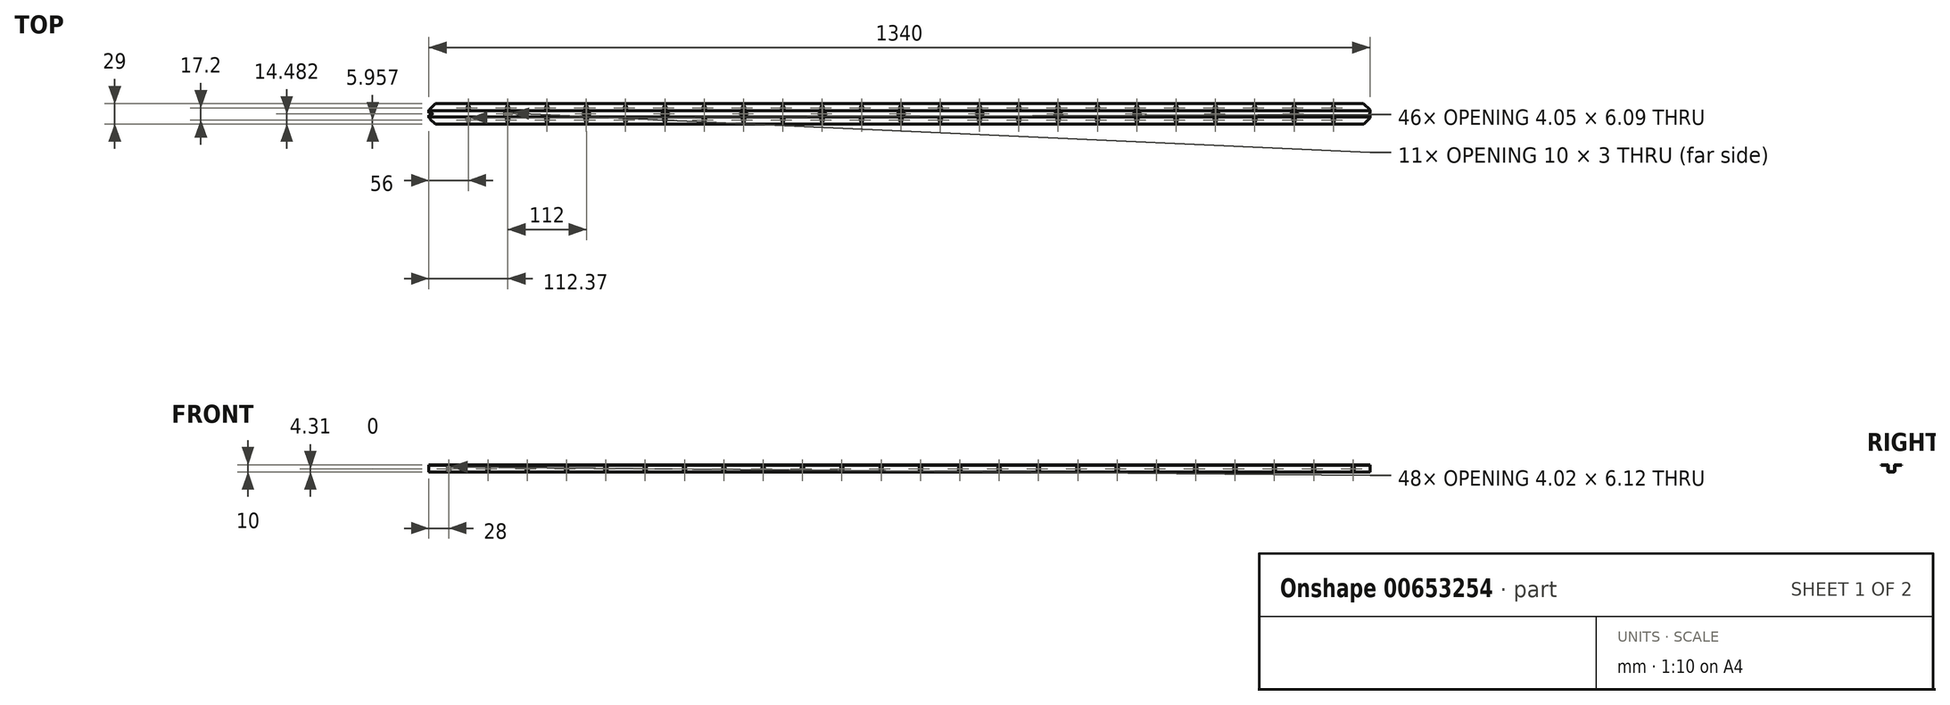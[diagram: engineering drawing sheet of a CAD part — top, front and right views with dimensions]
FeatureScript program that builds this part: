
annotation { "Feature Type Name" : "Feature", "Feature Type Description" : "" }
export const myFeature = defineFeature(function(context is Context, id is Id, definition is map)
    precondition{}
    {
        {
            var Q0;
            Q0=qCreatedBy(makeId("Right.planeOp"),FACE);
            var sketch = newSketch(context, id + "F0", { "sketchPlane" : qUnion([Q0])});
            skLineSegment(sketch, "E0", {"start": v(14.5, 5) * mm, "end": v(5.5, 5) * mm});
            skArc(sketch, "E1", {"start": v(5.5, 5) * mm, "mid": v(4.8, 4.7) * mm, "end": v(4.5, 4) * mm});
            skLineSegment(sketch, "E2", {"start": v(4.5, 4) * mm, "end": v(4.5, -4) * mm});
            skArc(sketch, "E3", {"start": v(4.5, -4) * mm, "mid": v(4.35, -4.35) * mm, "end": v(4, -4.5) * mm});
            skLineSegment(sketch, "E4", {"start": v(4, -4.5) * mm, "end": v(-4, -4.5) * mm});
            skArc(sketch, "E5", {"start": v(-4, -4.5) * mm, "mid": v(-4.35, -4.35) * mm, "end": v(-4.5, -4) * mm});
            skLineSegment(sketch, "E6", {"start": v(-4.5, -4) * mm, "end": v(-4.5, 4) * mm});
            skArc(sketch, "E7", {"start": v(-4.5, 4) * mm, "mid": v(-4.8, 4.7) * mm, "end": v(-5.5, 5) * mm});
            skLineSegment(sketch, "E8", {"start": v(-5.5, 5) * mm, "end": v(-14.5, 5) * mm});
            skLineSegment(sketch, "E9", {"start": v(-14.5, 5) * mm, "end": v(-14.5, 4.5) * mm});
            skLineSegment(sketch, "E10", {"start": v(-14.5, 4.5) * mm, "end": v(-5.5, 4.5) * mm});
            skArc(sketch, "E11", {"start": v(-5.5, 4.5) * mm, "mid": v(-5.15, 4.35) * mm, "end": v(-5, 4) * mm});
            skLineSegment(sketch, "E12", {"start": v(-5, 4) * mm, "end": v(-5, -4) * mm});
            skArc(sketch, "E13", {"start": v(-5, -4) * mm, "mid": v(-4.7, -4.7) * mm, "end": v(-4, -5) * mm});
            skLineSegment(sketch, "E14", {"start": v(-4, -5) * mm, "end": v(4, -5) * mm});
            skArc(sketch, "E15", {"start": v(4, -5) * mm, "mid": v(4.7, -4.7) * mm, "end": v(5, -4) * mm});
            skLineSegment(sketch, "E16", {"start": v(5, -4) * mm, "end": v(5, 4) * mm});
            skArc(sketch, "E17", {"start": v(5, 4) * mm, "mid": v(5.15, 4.35) * mm, "end": v(5.5, 4.5) * mm});
            skLineSegment(sketch, "E18", {"start": v(5.5, 4.5) * mm, "end": v(14.5, 4.5) * mm});
            skLineSegment(sketch, "E19", {"start": v(14.5, 4.5) * mm, "end": v(14.5, 5) * mm});
            skSolve(sketch);
        }
        {
            var Q0;
            Q0=qSketchRegion(id+"F0",true);
            extrude(context, id + "F1", {"entities" : qUnion([Q0]), "oppositeDirection" : true, "depth" : 1340 * mm, "offsetDistance" : 25 * mm});
        }
        {
            var Q0;
            Q0=makeQuery(id+"F1.opExtrude","SWEPT_FACE",FACE,{"disambiguationData":[OSD([sQuery(id+"F0.wireOp",EDGE,"E4")])]});
            var sketch = newSketch(context, id + "F2", { "sketchPlane" : qUnion([Q0])});
            skLineSegment(sketch, "E20.bottom", {"start": v(-1343.8, -1.5) * mm, "end": v(-1336.2, -1.5) * mm});
            skLineSegment(sketch, "E20.top", {"start": v(-1343.8, 1.5) * mm, "end": v(-1336.2, 1.5) * mm});
            skLineSegment(sketch, "E20.left", {"start": v(-1345, -0.3) * mm, "end": v(-1345, 0.3) * mm});
            skLineSegment(sketch, "E20.right", {"start": v(-1335, -0.3) * mm, "end": v(-1335, 0.3) * mm});
            skArc(sketch, "E21.filletArc", {"start": v(-1345, -0.3) * mm, "mid": v(-1344.65, -1.15) * mm, "end": v(-1343.8, -1.5) * mm});
            skArc(sketch, "E22.filletArc", {"start": v(-1343.8, 1.5) * mm, "mid": v(-1344.65, 1.15) * mm, "end": v(-1345, 0.3) * mm});
            skArc(sketch, "E23.filletArc", {"start": v(-1335, 0.3) * mm, "mid": v(-1335.35, 1.15) * mm, "end": v(-1336.2, 1.5) * mm});
            skArc(sketch, "E24.filletArc", {"start": v(-1336.2, -1.5) * mm, "mid": v(-1335.35, -1.15) * mm, "end": v(-1335, -0.3) * mm});
            skLineSegment(sketch, "E25.bottom", {"start": v(-1119.43, -1.52) * mm, "end": v(-1111.83, -1.52) * mm});
            skLineSegment(sketch, "E25.top", {"start": v(-1119.43, 1.48) * mm, "end": v(-1111.83, 1.48) * mm});
            skLineSegment(sketch, "E25.left", {"start": v(-1120.63, -0.32) * mm, "end": v(-1120.63, 0.28) * mm});
            skLineSegment(sketch, "E25.right", {"start": v(-1110.63, -0.32) * mm, "end": v(-1110.63, 0.28) * mm});
            skArc(sketch, "E26.filletArc", {"start": v(-1120.63, -0.32) * mm, "mid": v(-1120.28, -1.17) * mm, "end": v(-1119.43, -1.52) * mm});
            skArc(sketch, "E27.filletArc", {"start": v(-1119.43, 1.48) * mm, "mid": v(-1120.28, 1.13) * mm, "end": v(-1120.63, 0.28) * mm});
            skArc(sketch, "E28.filletArc", {"start": v(-1110.63, 0.28) * mm, "mid": v(-1110.98, 1.13) * mm, "end": v(-1111.83, 1.48) * mm});
            skArc(sketch, "E29.filletArc", {"start": v(-1111.83, -1.52) * mm, "mid": v(-1110.98, -1.17) * mm, "end": v(-1110.63, -0.32) * mm});
            skLineSegment(sketch, "E30.bottom", {"start": v(-1231.43, -1.52) * mm, "end": v(-1223.83, -1.52) * mm});
            skLineSegment(sketch, "E30.top", {"start": v(-1231.43, 1.48) * mm, "end": v(-1223.83, 1.48) * mm});
            skLineSegment(sketch, "E30.left", {"start": v(-1232.63, -0.32) * mm, "end": v(-1232.63, 0.28) * mm});
            skLineSegment(sketch, "E30.right", {"start": v(-1222.63, -0.32) * mm, "end": v(-1222.63, 0.28) * mm});
            skArc(sketch, "E31.filletArc", {"start": v(-1232.63, -0.32) * mm, "mid": v(-1232.28, -1.17) * mm, "end": v(-1231.43, -1.52) * mm});
            skArc(sketch, "E32.filletArc", {"start": v(-1231.43, 1.48) * mm, "mid": v(-1232.28, 1.13) * mm, "end": v(-1232.63, 0.28) * mm});
            skArc(sketch, "E33.filletArc", {"start": v(-1222.63, 0.28) * mm, "mid": v(-1222.98, 1.13) * mm, "end": v(-1223.83, 1.48) * mm});
            skArc(sketch, "E34.filletArc", {"start": v(-1223.83, -1.52) * mm, "mid": v(-1222.98, -1.17) * mm, "end": v(-1222.63, -0.32) * mm});
            skLineSegment(sketch, "E35.bottom", {"start": v(-1007.43, -1.52) * mm, "end": v(-999.83, -1.52) * mm});
            skLineSegment(sketch, "E35.top", {"start": v(-1007.43, 1.48) * mm, "end": v(-999.83, 1.48) * mm});
            skLineSegment(sketch, "E35.left", {"start": v(-1008.63, -0.32) * mm, "end": v(-1008.63, 0.28) * mm});
            skLineSegment(sketch, "E35.right", {"start": v(-998.63, -0.32) * mm, "end": v(-998.63, 0.28) * mm});
            skArc(sketch, "E36.filletArc", {"start": v(-1008.63, -0.32) * mm, "mid": v(-1008.28, -1.17) * mm, "end": v(-1007.43, -1.52) * mm});
            skArc(sketch, "E37.filletArc", {"start": v(-1007.43, 1.48) * mm, "mid": v(-1008.28, 1.13) * mm, "end": v(-1008.63, 0.28) * mm});
            skArc(sketch, "E38.filletArc", {"start": v(-998.63, 0.28) * mm, "mid": v(-998.98, 1.13) * mm, "end": v(-999.83, 1.48) * mm});
            skArc(sketch, "E39.filletArc", {"start": v(-999.83, -1.52) * mm, "mid": v(-998.98, -1.17) * mm, "end": v(-998.63, -0.32) * mm});
            skLineSegment(sketch, "E40.1.0.0", {"start": v(-895.43, -1.52) * mm, "end": v(-887.83, -1.52) * mm});
            skArc(sketch, "E40.1.0.1", {"start": v(-896.63, -0.32) * mm, "mid": v(-896.28, -1.17) * mm, "end": v(-895.43, -1.52) * mm});
            skLineSegment(sketch, "E40.1.0.2", {"start": v(-896.63, -0.32) * mm, "end": v(-896.63, 0.28) * mm});
            skArc(sketch, "E40.1.0.3", {"start": v(-895.43, 1.48) * mm, "mid": v(-896.28, 1.13) * mm, "end": v(-896.63, 0.28) * mm});
            skLineSegment(sketch, "E40.1.0.4", {"start": v(-895.43, 1.48) * mm, "end": v(-887.83, 1.48) * mm});
            skArc(sketch, "E40.1.0.5", {"start": v(-886.63, 0.28) * mm, "mid": v(-886.98, 1.13) * mm, "end": v(-887.83, 1.48) * mm});
            skLineSegment(sketch, "E40.1.0.6", {"start": v(-886.63, -0.32) * mm, "end": v(-886.63, 0.28) * mm});
            skArc(sketch, "E40.1.0.7", {"start": v(-887.83, -1.52) * mm, "mid": v(-886.98, -1.17) * mm, "end": v(-886.63, -0.32) * mm});
            skLineSegment(sketch, "E40.2.0.0", {"start": v(-783.43, -1.52) * mm, "end": v(-775.83, -1.52) * mm});
            skArc(sketch, "E40.2.0.1", {"start": v(-784.63, -0.32) * mm, "mid": v(-784.28, -1.17) * mm, "end": v(-783.43, -1.52) * mm});
            skLineSegment(sketch, "E40.2.0.2", {"start": v(-784.63, -0.32) * mm, "end": v(-784.63, 0.28) * mm});
            skArc(sketch, "E40.2.0.3", {"start": v(-783.43, 1.48) * mm, "mid": v(-784.28, 1.13) * mm, "end": v(-784.63, 0.28) * mm});
            skLineSegment(sketch, "E40.2.0.4", {"start": v(-783.43, 1.48) * mm, "end": v(-775.83, 1.48) * mm});
            skArc(sketch, "E40.2.0.5", {"start": v(-774.63, 0.28) * mm, "mid": v(-774.98, 1.13) * mm, "end": v(-775.83, 1.48) * mm});
            skLineSegment(sketch, "E40.2.0.6", {"start": v(-774.63, -0.32) * mm, "end": v(-774.63, 0.28) * mm});
            skArc(sketch, "E40.2.0.7", {"start": v(-775.83, -1.52) * mm, "mid": v(-774.98, -1.17) * mm, "end": v(-774.63, -0.32) * mm});
            skLineSegment(sketch, "E40.3.0.0", {"start": v(-671.43, -1.52) * mm, "end": v(-663.83, -1.52) * mm});
            skArc(sketch, "E40.3.0.1", {"start": v(-672.63, -0.32) * mm, "mid": v(-672.28, -1.17) * mm, "end": v(-671.43, -1.52) * mm});
            skLineSegment(sketch, "E40.3.0.2", {"start": v(-672.63, -0.32) * mm, "end": v(-672.63, 0.28) * mm});
            skArc(sketch, "E40.3.0.3", {"start": v(-671.43, 1.48) * mm, "mid": v(-672.28, 1.13) * mm, "end": v(-672.63, 0.28) * mm});
            skLineSegment(sketch, "E40.3.0.4", {"start": v(-671.43, 1.48) * mm, "end": v(-663.83, 1.48) * mm});
            skArc(sketch, "E40.3.0.5", {"start": v(-662.63, 0.28) * mm, "mid": v(-662.98, 1.13) * mm, "end": v(-663.83, 1.48) * mm});
            skLineSegment(sketch, "E40.3.0.6", {"start": v(-662.63, -0.32) * mm, "end": v(-662.63, 0.28) * mm});
            skArc(sketch, "E40.3.0.7", {"start": v(-663.83, -1.52) * mm, "mid": v(-662.98, -1.17) * mm, "end": v(-662.63, -0.32) * mm});
            skLineSegment(sketch, "E40.4.0.0", {"start": v(-559.43, -1.52) * mm, "end": v(-551.83, -1.52) * mm});
            skArc(sketch, "E40.4.0.1", {"start": v(-560.63, -0.32) * mm, "mid": v(-560.28, -1.17) * mm, "end": v(-559.43, -1.52) * mm});
            skLineSegment(sketch, "E40.4.0.2", {"start": v(-560.63, -0.32) * mm, "end": v(-560.63, 0.28) * mm});
            skArc(sketch, "E40.4.0.3", {"start": v(-559.43, 1.48) * mm, "mid": v(-560.28, 1.13) * mm, "end": v(-560.63, 0.28) * mm});
            skLineSegment(sketch, "E40.4.0.4", {"start": v(-559.43, 1.48) * mm, "end": v(-551.83, 1.48) * mm});
            skArc(sketch, "E40.4.0.5", {"start": v(-550.63, 0.28) * mm, "mid": v(-550.98, 1.13) * mm, "end": v(-551.83, 1.48) * mm});
            skLineSegment(sketch, "E40.4.0.6", {"start": v(-550.63, -0.32) * mm, "end": v(-550.63, 0.28) * mm});
            skArc(sketch, "E40.4.0.7", {"start": v(-551.83, -1.52) * mm, "mid": v(-550.98, -1.17) * mm, "end": v(-550.63, -0.32) * mm});
            skLineSegment(sketch, "E40.5.0.0", {"start": v(-447.43, -1.52) * mm, "end": v(-439.83, -1.52) * mm});
            skArc(sketch, "E40.5.0.1", {"start": v(-448.63, -0.32) * mm, "mid": v(-448.28, -1.17) * mm, "end": v(-447.43, -1.52) * mm});
            skLineSegment(sketch, "E40.5.0.2", {"start": v(-448.63, -0.32) * mm, "end": v(-448.63, 0.28) * mm});
            skArc(sketch, "E40.5.0.3", {"start": v(-447.43, 1.48) * mm, "mid": v(-448.28, 1.13) * mm, "end": v(-448.63, 0.28) * mm});
            skLineSegment(sketch, "E40.5.0.4", {"start": v(-447.43, 1.48) * mm, "end": v(-439.83, 1.48) * mm});
            skArc(sketch, "E40.5.0.5", {"start": v(-438.63, 0.28) * mm, "mid": v(-438.98, 1.13) * mm, "end": v(-439.83, 1.48) * mm});
            skLineSegment(sketch, "E40.5.0.6", {"start": v(-438.63, -0.32) * mm, "end": v(-438.63, 0.28) * mm});
            skArc(sketch, "E40.5.0.7", {"start": v(-439.83, -1.52) * mm, "mid": v(-438.98, -1.17) * mm, "end": v(-438.63, -0.32) * mm});
            skLineSegment(sketch, "E40.6.0.0", {"start": v(-335.43, -1.52) * mm, "end": v(-327.83, -1.52) * mm});
            skArc(sketch, "E40.6.0.1", {"start": v(-336.63, -0.32) * mm, "mid": v(-336.28, -1.17) * mm, "end": v(-335.43, -1.52) * mm});
            skLineSegment(sketch, "E40.6.0.2", {"start": v(-336.63, -0.32) * mm, "end": v(-336.63, 0.28) * mm});
            skArc(sketch, "E40.6.0.3", {"start": v(-335.43, 1.48) * mm, "mid": v(-336.28, 1.13) * mm, "end": v(-336.63, 0.28) * mm});
            skLineSegment(sketch, "E40.6.0.4", {"start": v(-335.43, 1.48) * mm, "end": v(-327.83, 1.48) * mm});
            skArc(sketch, "E40.6.0.5", {"start": v(-326.63, 0.28) * mm, "mid": v(-326.98, 1.13) * mm, "end": v(-327.83, 1.48) * mm});
            skLineSegment(sketch, "E40.6.0.6", {"start": v(-326.63, -0.32) * mm, "end": v(-326.63, 0.28) * mm});
            skArc(sketch, "E40.6.0.7", {"start": v(-327.83, -1.52) * mm, "mid": v(-326.98, -1.17) * mm, "end": v(-326.63, -0.32) * mm});
            skLineSegment(sketch, "E40.7.0.0", {"start": v(-223.43, -1.52) * mm, "end": v(-215.83, -1.52) * mm});
            skArc(sketch, "E40.7.0.1", {"start": v(-224.63, -0.32) * mm, "mid": v(-224.28, -1.17) * mm, "end": v(-223.43, -1.52) * mm});
            skLineSegment(sketch, "E40.7.0.2", {"start": v(-224.63, -0.32) * mm, "end": v(-224.63, 0.28) * mm});
            skArc(sketch, "E40.7.0.3", {"start": v(-223.43, 1.48) * mm, "mid": v(-224.28, 1.13) * mm, "end": v(-224.63, 0.28) * mm});
            skLineSegment(sketch, "E40.7.0.4", {"start": v(-223.43, 1.48) * mm, "end": v(-215.83, 1.48) * mm});
            skArc(sketch, "E40.7.0.5", {"start": v(-214.63, 0.28) * mm, "mid": v(-214.98, 1.13) * mm, "end": v(-215.83, 1.48) * mm});
            skLineSegment(sketch, "E40.7.0.6", {"start": v(-214.63, -0.32) * mm, "end": v(-214.63, 0.28) * mm});
            skArc(sketch, "E40.7.0.7", {"start": v(-215.83, -1.52) * mm, "mid": v(-214.98, -1.17) * mm, "end": v(-214.63, -0.32) * mm});
            skLineSegment(sketch, "E40.8.0.0", {"start": v(-111.43, -1.52) * mm, "end": v(-103.83, -1.52) * mm});
            skArc(sketch, "E40.8.0.1", {"start": v(-112.63, -0.32) * mm, "mid": v(-112.28, -1.17) * mm, "end": v(-111.43, -1.52) * mm});
            skLineSegment(sketch, "E40.8.0.2", {"start": v(-112.63, -0.32) * mm, "end": v(-112.63, 0.28) * mm});
            skArc(sketch, "E40.8.0.3", {"start": v(-111.43, 1.48) * mm, "mid": v(-112.28, 1.13) * mm, "end": v(-112.63, 0.28) * mm});
            skLineSegment(sketch, "E40.8.0.4", {"start": v(-111.43, 1.48) * mm, "end": v(-103.83, 1.48) * mm});
            skArc(sketch, "E40.8.0.5", {"start": v(-102.63, 0.28) * mm, "mid": v(-102.98, 1.13) * mm, "end": v(-103.83, 1.48) * mm});
            skLineSegment(sketch, "E40.8.0.6", {"start": v(-102.63, -0.32) * mm, "end": v(-102.63, 0.28) * mm});
            skArc(sketch, "E40.8.0.7", {"start": v(-103.83, -1.52) * mm, "mid": v(-102.98, -1.17) * mm, "end": v(-102.63, -0.32) * mm});
            skLineSegment(sketch, "E40.9.0.0", {"start": v(0.57, -1.52) * mm, "end": v(8.17, -1.52) * mm});
            skArc(sketch, "E40.9.0.1", {"start": v(-0.63, -0.32) * mm, "mid": v(-0.28, -1.17) * mm, "end": v(0.57, -1.52) * mm});
            skLineSegment(sketch, "E40.9.0.2", {"start": v(-0.63, -0.32) * mm, "end": v(-0.63, 0.28) * mm});
            skArc(sketch, "E40.9.0.3", {"start": v(0.57, 1.48) * mm, "mid": v(-0.28, 1.13) * mm, "end": v(-0.63, 0.28) * mm});
            skLineSegment(sketch, "E40.9.0.4", {"start": v(0.57, 1.48) * mm, "end": v(8.17, 1.48) * mm});
            skArc(sketch, "E40.9.0.5", {"start": v(9.37, 0.28) * mm, "mid": v(9.02, 1.13) * mm, "end": v(8.17, 1.48) * mm});
            skLineSegment(sketch, "E40.9.0.6", {"start": v(9.37, -0.32) * mm, "end": v(9.37, 0.28) * mm});
            skArc(sketch, "E40.9.0.7", {"start": v(8.17, -1.52) * mm, "mid": v(9.02, -1.17) * mm, "end": v(9.37, -0.32) * mm});
            skLineSegment(sketch, "E40.direction1", {"start": v(-998.63, -0.32) * mm, "end": v(-886.63, -0.32) * mm, "construction": true});
            skSolve(sketch);
        }
        {
            var Q0;
            Q0=qSketchRegion(id+"F2",true);
            extrude(context, id + "F3", {"entities" : qUnion([Q0]), "operationType" : NewBodyOperationType.REMOVE, "endBound" : BoundingType.THROUGH_ALL, "oppositeDirection" : true, "depth" : 25 * mm, "offsetDistance" : 25 * mm});
        }
        {
            var Q0;
            Q0=makeQuery(id+"F1.opExtrude","SWEPT_FACE",FACE,{"disambiguationData":[OSD([sQuery(id+"F0.wireOp",EDGE,"E12")])]});
            var sketch = newSketch(context, id + "F4", { "sketchPlane" : qUnion([Q0])});
            skEllipse(sketch, "E41", {"center": v(-1312, -0.69) * mm, "majorRadius": 3.06 * mm, "minorRadius": 2.01 * mm, "majorAxis": v(0, 1)});
            skEllipse(sketch, "E42.1.0.0", {"center": v(-1256, -0.69) * mm, "majorRadius": 3.06 * mm, "minorRadius": 2.01 * mm, "majorAxis": v(0, 1)});
            skEllipse(sketch, "E42.2.0.0", {"center": v(-1200, -0.69) * mm, "majorRadius": 3.06 * mm, "minorRadius": 2.01 * mm, "majorAxis": v(0, 1)});
            skEllipse(sketch, "E42.3.0.0", {"center": v(-1144, -0.69) * mm, "majorRadius": 3.06 * mm, "minorRadius": 2.01 * mm, "majorAxis": v(0, 1)});
            skEllipse(sketch, "E42.4.0.0", {"center": v(-1088, -0.69) * mm, "majorRadius": 3.06 * mm, "minorRadius": 2.01 * mm, "majorAxis": v(0, 1)});
            skEllipse(sketch, "E42.5.0.0", {"center": v(-1032, -0.69) * mm, "majorRadius": 3.06 * mm, "minorRadius": 2.01 * mm, "majorAxis": v(0, 1)});
            skEllipse(sketch, "E42.6.0.0", {"center": v(-976, -0.69) * mm, "majorRadius": 3.06 * mm, "minorRadius": 2.01 * mm, "majorAxis": v(0, 1)});
            skEllipse(sketch, "E42.7.0.0", {"center": v(-920, -0.69) * mm, "majorRadius": 3.06 * mm, "minorRadius": 2.01 * mm, "majorAxis": v(0, 1)});
            skEllipse(sketch, "E42.8.0.0", {"center": v(-864, -0.69) * mm, "majorRadius": 3.06 * mm, "minorRadius": 2.01 * mm, "majorAxis": v(0, 1)});
            skEllipse(sketch, "E42.9.0.0", {"center": v(-808, -0.69) * mm, "majorRadius": 3.06 * mm, "minorRadius": 2.01 * mm, "majorAxis": v(0, 1)});
            skEllipse(sketch, "E42.10.0.0", {"center": v(-752, -0.69) * mm, "majorRadius": 3.06 * mm, "minorRadius": 2.01 * mm, "majorAxis": v(0, 1)});
            skEllipse(sketch, "E42.11.0.0", {"center": v(-696, -0.69) * mm, "majorRadius": 3.06 * mm, "minorRadius": 2.01 * mm, "majorAxis": v(0, 1)});
            skEllipse(sketch, "E42.12.0.0", {"center": v(-640, -0.69) * mm, "majorRadius": 3.06 * mm, "minorRadius": 2.01 * mm, "majorAxis": v(0, 1)});
            skEllipse(sketch, "E42.13.0.0", {"center": v(-584, -0.69) * mm, "majorRadius": 3.06 * mm, "minorRadius": 2.01 * mm, "majorAxis": v(0, 1)});
            skEllipse(sketch, "E42.14.0.0", {"center": v(-528, -0.69) * mm, "majorRadius": 3.06 * mm, "minorRadius": 2.01 * mm, "majorAxis": v(0, 1)});
            skEllipse(sketch, "E42.15.0.0", {"center": v(-472, -0.69) * mm, "majorRadius": 3.06 * mm, "minorRadius": 2.01 * mm, "majorAxis": v(0, 1)});
            skEllipse(sketch, "E42.16.0.0", {"center": v(-416, -0.69) * mm, "majorRadius": 3.06 * mm, "minorRadius": 2.01 * mm, "majorAxis": v(0, 1)});
            skEllipse(sketch, "E42.17.0.0", {"center": v(-360, -0.69) * mm, "majorRadius": 3.06 * mm, "minorRadius": 2.01 * mm, "majorAxis": v(0, 1)});
            skEllipse(sketch, "E42.18.0.0", {"center": v(-304, -0.69) * mm, "majorRadius": 3.06 * mm, "minorRadius": 2.01 * mm, "majorAxis": v(0, 1)});
            skEllipse(sketch, "E42.19.0.0", {"center": v(-248, -0.69) * mm, "majorRadius": 3.06 * mm, "minorRadius": 2.01 * mm, "majorAxis": v(0, 1)});
            skEllipse(sketch, "E42.20.0.0", {"center": v(-192, -0.69) * mm, "majorRadius": 3.06 * mm, "minorRadius": 2.01 * mm, "majorAxis": v(0, 1)});
            skEllipse(sketch, "E42.21.0.0", {"center": v(-136, -0.69) * mm, "majorRadius": 3.06 * mm, "minorRadius": 2.01 * mm, "majorAxis": v(0, 1)});
            skEllipse(sketch, "E42.22.0.0", {"center": v(-80, -0.69) * mm, "majorRadius": 3.06 * mm, "minorRadius": 2.01 * mm, "majorAxis": v(0, 1)});
            skEllipse(sketch, "E42.23.0.0", {"center": v(-24, -0.69) * mm, "majorRadius": 3.06 * mm, "minorRadius": 2.01 * mm, "majorAxis": v(0, 1)});
            skLineSegment(sketch, "E42.direction1", {"start": v(-1340, -0.69) * mm, "end": v(-1284, -0.69) * mm, "construction": true});
            skSolve(sketch);
        }
        {
            var Q0;
            Q0=qSketchRegion(id+"F4",true);
            extrude(context, id + "F5", {"entities" : qUnion([Q0]), "operationType" : NewBodyOperationType.REMOVE, "oppositeDirection" : true, "depth" : 15 * mm, "offsetDistance" : 25 * mm});
        }
        {
            var Q0;
            Q0=makeQuery(id+"F1.opExtrude","SWEPT_FACE",FACE,{"disambiguationData":[OSD([sQuery(id+"F0.wireOp",EDGE,"E8")])]});
            var sketch = newSketch(context, id + "F6", { "sketchPlane" : qUnion([Q0])});
            skEllipse(sketch, "E43", {"center": v(-1340, -8.54) * mm, "majorRadius": 3.04 * mm, "minorRadius": 2.03 * mm, "majorAxis": v(0, -1)});
            skEllipse(sketch, "E44.0.1.0", {"center": v(-1340, 8.66) * mm, "majorRadius": 3.04 * mm, "minorRadius": 2.03 * mm, "majorAxis": v(0, -1)});
            skEllipse(sketch, "E44.1.0.0", {"center": v(-1284, -8.54) * mm, "majorRadius": 3.04 * mm, "minorRadius": 2.03 * mm, "majorAxis": v(0, -1)});
            skEllipse(sketch, "E44.1.1.0", {"center": v(-1284, 8.66) * mm, "majorRadius": 3.04 * mm, "minorRadius": 2.03 * mm, "majorAxis": v(0, -1)});
            skEllipse(sketch, "E44.2.0.0", {"center": v(-1228, -8.54) * mm, "majorRadius": 3.04 * mm, "minorRadius": 2.03 * mm, "majorAxis": v(0, -1)});
            skEllipse(sketch, "E44.2.1.0", {"center": v(-1228, 8.66) * mm, "majorRadius": 3.04 * mm, "minorRadius": 2.03 * mm, "majorAxis": v(0, -1)});
            skEllipse(sketch, "E44.3.0.0", {"center": v(-1172, -8.54) * mm, "majorRadius": 3.04 * mm, "minorRadius": 2.03 * mm, "majorAxis": v(0, -1)});
            skEllipse(sketch, "E44.3.1.0", {"center": v(-1172, 8.66) * mm, "majorRadius": 3.04 * mm, "minorRadius": 2.03 * mm, "majorAxis": v(0, -1)});
            skEllipse(sketch, "E44.4.0.0", {"center": v(-1116, -8.54) * mm, "majorRadius": 3.04 * mm, "minorRadius": 2.03 * mm, "majorAxis": v(0, -1)});
            skEllipse(sketch, "E44.4.1.0", {"center": v(-1116, 8.66) * mm, "majorRadius": 3.04 * mm, "minorRadius": 2.03 * mm, "majorAxis": v(0, -1)});
            skEllipse(sketch, "E44.5.0.0", {"center": v(-1060, -8.54) * mm, "majorRadius": 3.04 * mm, "minorRadius": 2.03 * mm, "majorAxis": v(0, -1)});
            skEllipse(sketch, "E44.5.1.0", {"center": v(-1060, 8.66) * mm, "majorRadius": 3.04 * mm, "minorRadius": 2.03 * mm, "majorAxis": v(0, -1)});
            skEllipse(sketch, "E44.6.0.0", {"center": v(-1004, -8.54) * mm, "majorRadius": 3.04 * mm, "minorRadius": 2.03 * mm, "majorAxis": v(0, -1)});
            skEllipse(sketch, "E44.6.1.0", {"center": v(-1004, 8.66) * mm, "majorRadius": 3.04 * mm, "minorRadius": 2.03 * mm, "majorAxis": v(0, -1)});
            skEllipse(sketch, "E44.7.0.0", {"center": v(-948, -8.54) * mm, "majorRadius": 3.04 * mm, "minorRadius": 2.03 * mm, "majorAxis": v(0, -1)});
            skEllipse(sketch, "E44.7.1.0", {"center": v(-948, 8.66) * mm, "majorRadius": 3.04 * mm, "minorRadius": 2.03 * mm, "majorAxis": v(0, -1)});
            skEllipse(sketch, "E44.8.0.0", {"center": v(-892, -8.54) * mm, "majorRadius": 3.04 * mm, "minorRadius": 2.03 * mm, "majorAxis": v(0, -1)});
            skEllipse(sketch, "E44.8.1.0", {"center": v(-892, 8.66) * mm, "majorRadius": 3.04 * mm, "minorRadius": 2.03 * mm, "majorAxis": v(0, -1)});
            skEllipse(sketch, "E44.9.0.0", {"center": v(-836, -8.54) * mm, "majorRadius": 3.04 * mm, "minorRadius": 2.03 * mm, "majorAxis": v(0, -1)});
            skEllipse(sketch, "E44.9.1.0", {"center": v(-836, 8.66) * mm, "majorRadius": 3.04 * mm, "minorRadius": 2.03 * mm, "majorAxis": v(0, -1)});
            skEllipse(sketch, "E44.10.0.0", {"center": v(-780, -8.54) * mm, "majorRadius": 3.04 * mm, "minorRadius": 2.03 * mm, "majorAxis": v(0, -1)});
            skEllipse(sketch, "E44.10.1.0", {"center": v(-780, 8.66) * mm, "majorRadius": 3.04 * mm, "minorRadius": 2.03 * mm, "majorAxis": v(0, -1)});
            skEllipse(sketch, "E44.11.0.0", {"center": v(-724, -8.54) * mm, "majorRadius": 3.04 * mm, "minorRadius": 2.03 * mm, "majorAxis": v(0, -1)});
            skEllipse(sketch, "E44.11.1.0", {"center": v(-724, 8.66) * mm, "majorRadius": 3.04 * mm, "minorRadius": 2.03 * mm, "majorAxis": v(0, -1)});
            skEllipse(sketch, "E44.12.0.0", {"center": v(-668, -8.54) * mm, "majorRadius": 3.04 * mm, "minorRadius": 2.03 * mm, "majorAxis": v(0, -1)});
            skEllipse(sketch, "E44.12.1.0", {"center": v(-668, 8.66) * mm, "majorRadius": 3.04 * mm, "minorRadius": 2.03 * mm, "majorAxis": v(0, -1)});
            skEllipse(sketch, "E44.13.0.0", {"center": v(-612, -8.54) * mm, "majorRadius": 3.04 * mm, "minorRadius": 2.03 * mm, "majorAxis": v(0, -1)});
            skEllipse(sketch, "E44.13.1.0", {"center": v(-612, 8.66) * mm, "majorRadius": 3.04 * mm, "minorRadius": 2.03 * mm, "majorAxis": v(0, -1)});
            skEllipse(sketch, "E44.14.0.0", {"center": v(-556, -8.54) * mm, "majorRadius": 3.04 * mm, "minorRadius": 2.03 * mm, "majorAxis": v(0, -1)});
            skEllipse(sketch, "E44.14.1.0", {"center": v(-556, 8.66) * mm, "majorRadius": 3.04 * mm, "minorRadius": 2.03 * mm, "majorAxis": v(0, -1)});
            skEllipse(sketch, "E44.15.0.0", {"center": v(-500, -8.54) * mm, "majorRadius": 3.04 * mm, "minorRadius": 2.03 * mm, "majorAxis": v(0, -1)});
            skEllipse(sketch, "E44.15.1.0", {"center": v(-500, 8.66) * mm, "majorRadius": 3.04 * mm, "minorRadius": 2.03 * mm, "majorAxis": v(0, -1)});
            skEllipse(sketch, "E44.16.0.0", {"center": v(-444, -8.54) * mm, "majorRadius": 3.04 * mm, "minorRadius": 2.03 * mm, "majorAxis": v(0, -1)});
            skEllipse(sketch, "E44.16.1.0", {"center": v(-444, 8.66) * mm, "majorRadius": 3.04 * mm, "minorRadius": 2.03 * mm, "majorAxis": v(0, -1)});
            skEllipse(sketch, "E44.17.0.0", {"center": v(-388, -8.54) * mm, "majorRadius": 3.04 * mm, "minorRadius": 2.03 * mm, "majorAxis": v(0, -1)});
            skEllipse(sketch, "E44.17.1.0", {"center": v(-388, 8.66) * mm, "majorRadius": 3.04 * mm, "minorRadius": 2.03 * mm, "majorAxis": v(0, -1)});
            skEllipse(sketch, "E44.18.0.0", {"center": v(-332, -8.54) * mm, "majorRadius": 3.04 * mm, "minorRadius": 2.03 * mm, "majorAxis": v(0, -1)});
            skEllipse(sketch, "E44.18.1.0", {"center": v(-332, 8.66) * mm, "majorRadius": 3.04 * mm, "minorRadius": 2.03 * mm, "majorAxis": v(0, -1)});
            skEllipse(sketch, "E44.19.0.0", {"center": v(-276, -8.54) * mm, "majorRadius": 3.04 * mm, "minorRadius": 2.03 * mm, "majorAxis": v(0, -1)});
            skEllipse(sketch, "E44.19.1.0", {"center": v(-276, 8.66) * mm, "majorRadius": 3.04 * mm, "minorRadius": 2.03 * mm, "majorAxis": v(0, -1)});
            skEllipse(sketch, "E44.20.0.0", {"center": v(-220, -8.54) * mm, "majorRadius": 3.04 * mm, "minorRadius": 2.03 * mm, "majorAxis": v(0, -1)});
            skEllipse(sketch, "E44.20.1.0", {"center": v(-220, 8.66) * mm, "majorRadius": 3.04 * mm, "minorRadius": 2.03 * mm, "majorAxis": v(0, -1)});
            skEllipse(sketch, "E44.21.0.0", {"center": v(-164, -8.54) * mm, "majorRadius": 3.04 * mm, "minorRadius": 2.03 * mm, "majorAxis": v(0, -1)});
            skEllipse(sketch, "E44.21.1.0", {"center": v(-164, 8.66) * mm, "majorRadius": 3.04 * mm, "minorRadius": 2.03 * mm, "majorAxis": v(0, -1)});
            skEllipse(sketch, "E44.22.0.0", {"center": v(-108, -8.54) * mm, "majorRadius": 3.04 * mm, "minorRadius": 2.03 * mm, "majorAxis": v(0, -1)});
            skEllipse(sketch, "E44.22.1.0", {"center": v(-108, 8.66) * mm, "majorRadius": 3.04 * mm, "minorRadius": 2.03 * mm, "majorAxis": v(0, -1)});
            skEllipse(sketch, "E44.23.0.0", {"center": v(-52, -8.54) * mm, "majorRadius": 3.04 * mm, "minorRadius": 2.03 * mm, "majorAxis": v(0, -1)});
            skEllipse(sketch, "E44.23.1.0", {"center": v(-52, 8.66) * mm, "majorRadius": 3.04 * mm, "minorRadius": 2.03 * mm, "majorAxis": v(0, -1)});
            skLineSegment(sketch, "E44.direction1", {"start": v(-1340, -8.54) * mm, "end": v(-1284, -8.54) * mm, "construction": true});
            skLineSegment(sketch, "E44.direction2", {"start": v(-1340, -8.54) * mm, "end": v(-1340, 8.66) * mm, "construction": true});
            skSolve(sketch);
        }
        {
            var Q0;
            Q0=qSketchRegion(id+"F6",true);
            extrude(context, id + "F7", {"entities" : qUnion([Q0]), "operationType" : NewBodyOperationType.REMOVE, "endBound" : BoundingType.THROUGH_ALL, "oppositeDirection" : true, "depth" : 25 * mm, "offsetDistance" : 25 * mm});
        }
        {
            var Q0;
            Q0=makeQuery(id+"F1.opExtrude","SWEPT_FACE",FACE,{"disambiguationData":[OSD([sQuery(id+"F0.wireOp",EDGE,"E0")])]});
            var sketch = newSketch(context, id + "F8", { "sketchPlane" : qUnion([Q0])});
            skLineSegment(sketch, "E45", {"start": v(0, 5.5) * mm, "end": v(-9.01, 14.5) * mm});
            skLineSegment(sketch, "E46", {"start": v(-1340, 5.5) * mm, "end": v(-1331.01, 14.5) * mm});
            skSolve(sketch);
        }
        {
            var Q0;
            Q0=makeQuery(id+"F1.opExtrude","SWEPT_FACE",FACE,{"disambiguationData":[OSD([sQuery(id+"F0.wireOp",EDGE,"E8")])]});
            var sketch = newSketch(context, id + "F9", { "sketchPlane" : qUnion([Q0])});
            skLineSegment(sketch, "E47", {"start": v(0, -5.5) * mm, "end": v(-8.99, -14.5) * mm});
            skLineSegment(sketch, "E48", {"start": v(-1340, -5.5) * mm, "end": v(-1331, -14.5) * mm});
            skSolve(sketch);
        }
        {
            var Q0;
            {var subQ1=sQuery(id+"F0.wireOp",EDGE,"E8");var subQ6=makeQuery(id+"F1.opExtrude","CAP_EDGE",EDGE,{"disambiguationData":[OSD([subQ1])],"isStart":false});Q0=makeQuery(id+"F9.imprint","IMPRINT",FACE,{"disambiguationData":[TD([[makeQuery(id+"F9.imprint","IMPRINT",EDGE,{"derivedFrom":subQ6}),1.0]])]});}
            var Q1;
            {var subQ0=sQuery(id+"F9.wireOp",EDGE,"E47");Q1=makeQuery(id+"F9.imprint","IMPRINT",FACE,{"disambiguationData":[TD([[makeQuery(id+"F9.imprint","IMPRINT",EDGE,{"derivedFrom":subQ0}),1.0]])]});}
            extrude(context, id + "F10", {"entities" : qUnion([Q0, Q1]), "operationType" : NewBodyOperationType.REMOVE, "endBound" : BoundingType.THROUGH_ALL, "oppositeDirection" : true, "depth" : 25 * mm, "offsetDistance" : 25 * mm});
        }
        {
            var Q0;
            {var subQ0=sQuery(id+"F8.wireOp",EDGE,"E45");Q0=makeQuery(id+"F8.imprint","IMPRINT",FACE,{"disambiguationData":[TD([[makeQuery(id+"F8.imprint","IMPRINT",EDGE,{"derivedFrom":subQ0}),-1.0]])]});}
            var Q1;
            {var subQ0=sQuery(id+"F8.wireOp",EDGE,"E46");var subQ5=sQuery(id+"F6.wireOp",EDGE,"E44.0.1.0");var subQ6=makeQuery(id+"F7.boolean.opBoolean","COPY",EDGE,{"derivedFrom":makeQuery(id+"F7.opExtrude","CAP_EDGE",EDGE,{"disambiguationData":[OSD([subQ5])],"isStart":true})});var subQ7=makeQuery(id+"F8.imprint","INTERSECT",VERTEX,{"disambiguationData":[OD(1.0)],"derivedFrom":[subQ6,subQ0]});Q1=makeQuery(id+"F8.imprint","IMPRINT",FACE,{"disambiguationData":[TD([[makeQuery(id+"F8.imprint","IMPRINT",EDGE,{"disambiguationData":[TD([[subQ7,-1.0]])],"derivedFrom":subQ0}),1.0]])]});}
            extrude(context, id + "F11", {"entities" : qUnion([Q0, Q1]), "operationType" : NewBodyOperationType.REMOVE, "endBound" : BoundingType.THROUGH_ALL, "oppositeDirection" : true, "depth" : 25 * mm, "offsetDistance" : 25 * mm});
        }
    });
